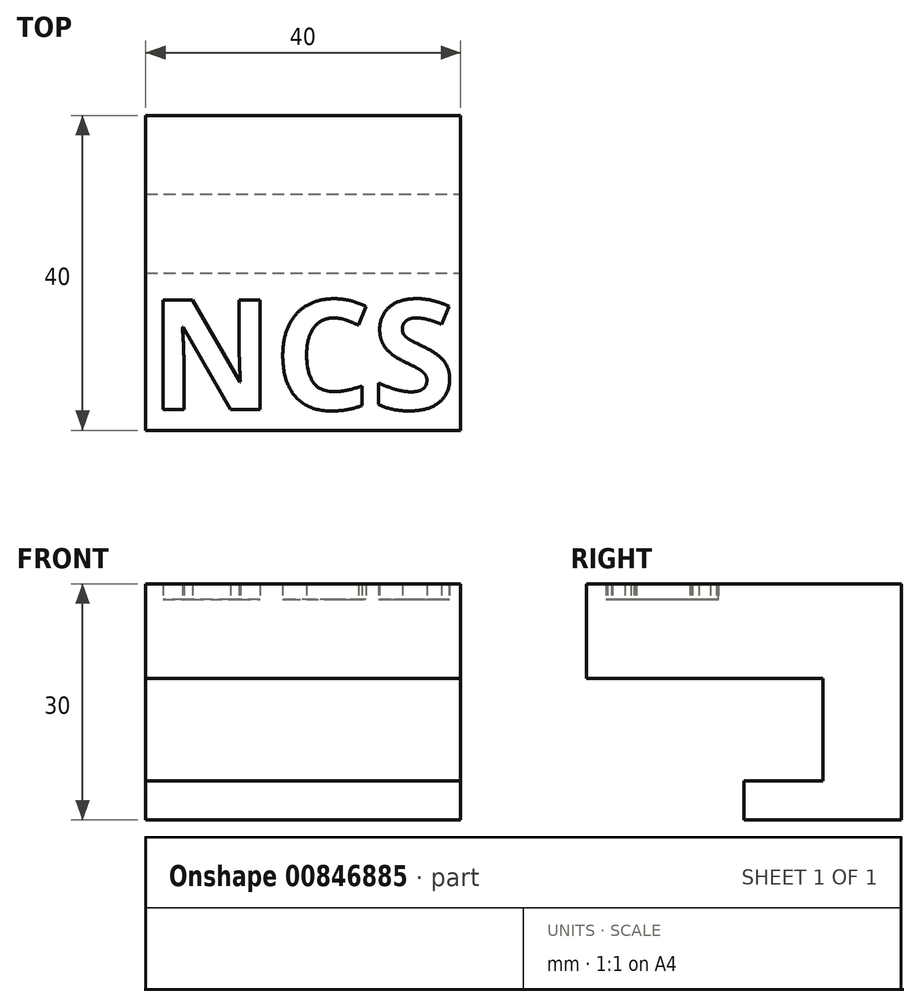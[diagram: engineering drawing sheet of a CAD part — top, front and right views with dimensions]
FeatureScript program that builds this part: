
annotation { "Feature Type Name" : "Feature", "Feature Type Description" : "" }
export const myFeature = defineFeature(function(context is Context, id is Id, definition is map)
    precondition{}
    {
        {
            var Q0;
            Q0=qCreatedBy(makeId("Top.planeOp"),FACE);
            var sketch = newSketch(context, id + "F0", { "sketchPlane" : qUnion([Q0])});
            skLineSegment(sketch, "E0.bottom", {"start": v(-20, 20) * mm, "end": v(20, 20) * mm});
            skLineSegment(sketch, "E0.top", {"start": v(-20, -20) * mm, "end": v(20, -20) * mm});
            skLineSegment(sketch, "E0.left", {"start": v(-20, 20) * mm, "end": v(-20, -20) * mm});
            skLineSegment(sketch, "E0.right", {"start": v(20, 20) * mm, "end": v(20, -20) * mm});
            skPoint(sketch, "E0.middle", {"position": v(0, 0) * mm});
            skLineSegment(sketch, "E1.top", {"start": v(-20, 10) * mm, "end": v(20, 10) * mm});
            skLineSegment(sketch, "E1.left", {"start": v(-20, 20) * mm, "end": v(-20, 10) * mm});
            skLineSegment(sketch, "E1.right", {"start": v(20, 20) * mm, "end": v(20, 10) * mm});
            skLineSegment(sketch, "E2.top", {"start": v(-20, 0) * mm, "end": v(20, 0) * mm});
            skLineSegment(sketch, "E2.left", {"start": v(-20, 20) * mm, "end": v(-20, 0) * mm});
            skLineSegment(sketch, "E2.right", {"start": v(20, 20) * mm, "end": v(20, 0) * mm});
            skText(sketch, "E3", { "text": "NCS", "fontName": "OpenSans-Bold.ttf"});
            const initialGuessF0  = {"E3": [-0.01953, -0.01735, 1, 0, 0.014]};
            skSetInitialGuess(sketch, initialGuessF0);
            skSolve(sketch);
        }
        {
            var Q0;
            {var subQ0=sQuery(id+"F0.wireOp",EDGE,"E1.top");Q0=makeQuery(id+"F0.imprint","IMPRINT",FACE,{"disambiguationData":[TD([[makeQuery(id+"F0.imprint","IMPRINT",EDGE,{"derivedFrom":subQ0}),1.0]])]});}
            var Q1;
            {var subQ0=sQuery(id+"F0.wireOp",EDGE,"E1.top");Q1=makeQuery(id+"F0.imprint","IMPRINT",FACE,{"disambiguationData":[TD([[makeQuery(id+"F0.imprint","IMPRINT",EDGE,{"derivedFrom":subQ0}),-1.0]])]});}
            extrude(context, id + "F1", {"entities" : qUnion([Q0, Q1]), "oppositeDirection" : true, "depth" : 5 * mm, "offsetDistance" : 25 * mm});
        }
        {
            var Q0;
            {var subQ0=sQuery(id+"F0.wireOp",EDGE,"E1.top");Q0=makeQuery(id+"F0.imprint","IMPRINT",FACE,{"disambiguationData":[TD([[makeQuery(id+"F0.imprint","IMPRINT",EDGE,{"derivedFrom":subQ0}),1.0]])]});}
            extrude(context, id + "F2", {"entities" : qUnion([Q0]), "operationType" : NewBodyOperationType.ADD, "depth" : 13 * mm, "offsetDistance" : 25 * mm});
        }
        {
            var Q0;
            Q0=makeQuery(id+"F0.imprint","IMPRINT",FACE,{"disambiguationData":[TD([[makeQuery(id+"F0.imprint","IMPRINT",EDGE,{"derivedFrom":sQuery(id+"F0.wireOp",EDGE,"E0.top")}),1.0]])]});
            var Q1;
            {var subQ0=sQuery(id+"F0.wireOp",EDGE,"E1.top");Q1=makeQuery(id+"F0.imprint","IMPRINT",FACE,{"disambiguationData":[TD([[makeQuery(id+"F0.imprint","IMPRINT",EDGE,{"derivedFrom":subQ0}),-1.0]])]});}
            var Q2;
            {var subQ0=sQuery(id+"F0.wireOp",EDGE,"E1.top");Q2=makeQuery(id+"F0.imprint","IMPRINT",FACE,{"disambiguationData":[TD([[makeQuery(id+"F0.imprint","IMPRINT",EDGE,{"derivedFrom":subQ0}),1.0]])]});}
            extrude(context, id + "F3", {"entities" : qUnion([Q0, Q1, Q2]), "operationType" : NewBodyOperationType.ADD, "depth" : 25 * mm, "offsetDistance" : 25 * mm, "hasSecondDirection" : true, "secondDirectionOppositeDirection" : false, "secondDirectionDepth" : 13 * mm});
        }
        {
            var Q0;
            Q0=makeQuery(id+"F0.imprint","IMPRINT",FACE,{"disambiguationData":[TD([[makeQuery(id+"F0.imprint","IMPRINT",EDGE,{"derivedFrom":sQuery(id+"F0.wireOp",EDGE,"E3.sketch_text.stroke-0")}),-1.0]])]});
            var Q1;
            Q1=makeQuery(id+"F0.imprint","IMPRINT",FACE,{"disambiguationData":[TD([[makeQuery(id+"F0.imprint","IMPRINT",EDGE,{"derivedFrom":sQuery(id+"F0.wireOp",EDGE,"E3.sketch_text.stroke-14")}),-1.0]])]});
            var Q2;
            Q2=makeQuery(id+"F0.imprint","IMPRINT",FACE,{"disambiguationData":[TD([[makeQuery(id+"F0.imprint","IMPRINT",EDGE,{"derivedFrom":sQuery(id+"F0.wireOp",EDGE,"E3.sketch_text.stroke-29")}),-1.0]])]});
            extrude(context, id + "F4", {"entities" : qUnion([Q0, Q1, Q2]), "operationType" : NewBodyOperationType.ADD, "depth" : 23 * mm, "offsetDistance" : 25 * mm, "hasSecondDirection" : true, "secondDirectionOppositeDirection" : true, "secondDirectionDepth" : -13 * mm});
        }
    });
